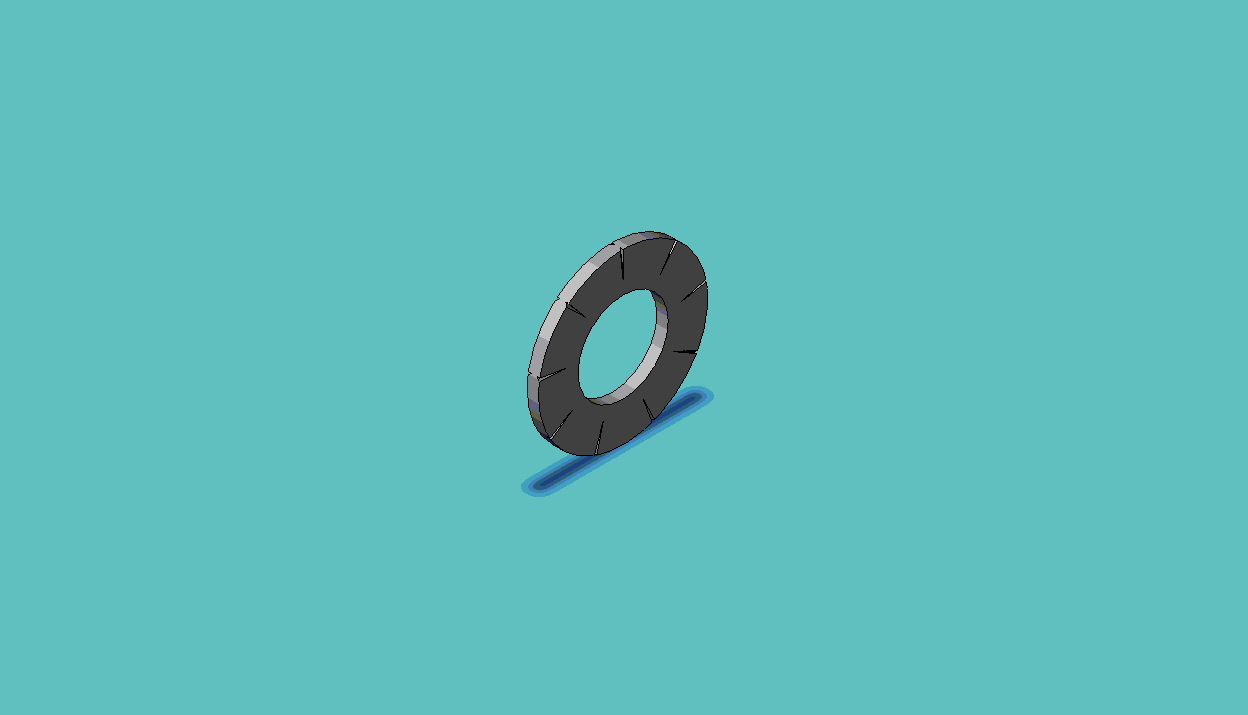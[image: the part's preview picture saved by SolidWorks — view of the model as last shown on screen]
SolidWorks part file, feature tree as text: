
SOLIDWORKS PART (.sldprt)
format: sldprt  version: not decoded by parser v0  size: 217,600 bytes
history: native  units: mm
features: sketch x7, plane x6, mirror x2, pattern_circular x2, material x1, extrude x1 + 2 further entries (+11 scaffold rows collapsed; 1 parser-record rows omitted)
feature tree (33):
  scaffold x11  (default folders/planes/origin — collapsed)
  material  "Material <not specified>"
  plane  "Plane1"
  plane  "Plane2"
  plane  "Plane3"
  parser-record x1  (decoder bookkeeping rows leaked as tree rows — omitted from the tree; the rows remain in map.json)
  extrude  "Base-Extrude"  [1 undecoded]
  sketch  "Sketch1"  dims[InsideDia=3.2mm OutsideDia=6.0mm Thickness=0.4mm D2=10.0mm D3=1.0deg D4=1.0deg]
  mirror  "TypeA2"
  sketch  "Sketch4"  dims[D1=0.1mm D2=0.1mm]
  sketch  "Sketch3"  dims[D1=2.062mm]
  sketch  "Sketch5"
  pattern_circular  "TypeAPattern"  Count=9 Angle=360deg NumTeeth=9
  plane  "Plane4"  Offset=3mm
  plane  "Plane5"  Offset=0.2mm
  plane  "Plane6"  Offset=1.52mm
  sketch  "Sketch6"  dims[D1=2.524mm]
  sketch  "Sketch7"  dims[D1=0.1mm D2=0.1mm]
  sketch  "Sketch8"
  mirror  "TypeJ3"
  pattern_circular  "TypeJPattern"  Count=7 Angle=360deg NumTeeth=7
  "ConfigurationName"  CopiedFlag=1
  "ConfigurationName"  CopiedFlag=0
decode coverage: 7 of 12 modeling features carry decoded parameters; 2 rows unclassified (native names shown)
note: 1 parameter value undecoded
note: suppression state not decoded; provenance and decode notes live in map.json
